# Revit family: VENTS-VS
name_source: partatom
category: Mechanical Equipment
units: mm (PartAtom-declared; Revit-internal decimal feet)

## family parameters
Always vertical = Yes
Classification = None
Cut with Voids When Loaded = No
OmniClass Number = 23.75.35.17.11
OmniClass Title = Fans for Air Ductwork
Part Type = Breaks Into
Room Calculation Point = No
Round Connector Dimension = Use Diameter
Shared = No
Work Plane-Based = No

## types (19) — shared parameters
Casing Material = Fan Zinc
Description = Inline centrifugal fan in sound insulated casing
Family Version = 1.0
Load Classification = HVAC
Maintenance Zone Material = Maintenance Zone
Manufacturer = Vents
Plastic Material = Polypropylene Black
Power Factor = 1
Protection rating = IPX4
URL = https://ventilation-system.com
eH = 75 mm
eL = 75 mm

## per-type parameters (varying)
| type | A | Apparent Power | Connection H | Connection W | Current | Din | Maintenance Zone Depth | Maximum Air Flow Directly | Maximum Air Flow Perpendicularly | Model | Noise Level at 3 m (dBa) | Number of Poles | Power | RPM (min-1) | Transported Air Temperature (°C) | Type Comments | Voltage | Weight | conA | gsD |
| VS 355 4E (50Hz) | 520 mm  [stored 1.70604 ft] | 245 VA | 445 mm  [stored 1.45997 ft] | 445 mm  [stored 1.45997 ft] | 1 A | 260 mm  [stored 0.853018 ft] | 520 mm  [stored 1.70604 ft] | 2650 m³/h | 2890 m³/h | VS 355 4E | 54 | 1 | 245 W | 1420 | -25...+50 | Inline centrifugal fan VS 355 4E | 230 V | 25.00 kg | 260 mm  [stored 0.853018 ft] | 260 mm  [stored 0.853018 ft] |
| VS 355 4D (Star 50Hz) | 520 mm  [stored 1.70604 ft] | 230 VA | 445 mm  [stored 1.45997 ft] | 445 mm  [stored 1.45997 ft] | 1 A | 260 mm  [stored 0.853018 ft] | 520 mm  [stored 1.70604 ft] | 2380 m³/h | 2660 m³/h | VS 355 4D | 53 | 3 | 230 W | 1400 | -25...+70 | Inline centrifugal fan VS 355 4D | 400 V | 25.00 kg | 260 mm  [stored 0.853018 ft] | 260 mm  [stored 0.853018 ft] |
| VS 355 4D (Star 60Hz) | 520 mm  [stored 1.70604 ft] | 235 VA | 445 mm  [stored 1.45997 ft] | 445 mm  [stored 1.45997 ft] | 1 A | 260 mm  [stored 0.853018 ft] | 520 mm  [stored 1.70604 ft] | 2580 m³/h | 2815 m³/h | VS 355 4D | 55 | 3 | 235 W | 1600 | -25...+65 | Inline centrifugal fan VS 355 4D | 400 V | 25.00 kg | 260 mm  [stored 0.853018 ft] | 260 mm  [stored 0.853018 ft] |
| VS 400 4E (50Hz) | 690 mm  [stored 2.26378 ft] | 480 VA | 615 mm  [stored 2.01772 ft] | 615 mm  [stored 2.01772 ft] | 2 A | 345 mm  [stored 1.13189 ft] | 690 mm  [stored 2.26378 ft] | 3535 m³/h | 3750 m³/h | VS 400 4E | 51 | 1 | 480 W | 1370 | -40...+80 | Inline centrifugal fan VS 400 4E | 230 V | 39.00 kg | 345 mm  [stored 1.13189 ft] | 345 mm  [stored 1.13189 ft] |
| VS 400 4E (60Hz) | 690 mm  [stored 2.26378 ft] | 700 VA | 615 mm  [stored 2.01772 ft] | 615 mm  [stored 2.01772 ft] | 3 A | 345 mm  [stored 1.13189 ft] | 690 mm  [stored 2.26378 ft] | 4015 m³/h | 4310 m³/h | VS 400 4E | 52 | 1 | 700 W | 1460 | -40...+55 | Inline centrifugal fan VS 400 4E | 230 V | 39.00 kg | 345 mm  [stored 1.13189 ft] | 345 mm  [stored 1.13189 ft] |
| VS 400 4D (Delta 50Hz) | 690 mm  [stored 2.26378 ft] | 515 VA | 615 mm  [stored 2.01772 ft] | 615 mm  [stored 2.01772 ft] | 1 A | 345 mm  [stored 1.13189 ft] | 690 mm  [stored 2.26378 ft] | 3740 m³/h | 3950 m³/h | VS 400 4D (Delta) | 51 | 3 | 515 W | 1415 | -40...+60 | Inline centrifugal fan VS 400 4D (Delta) | 400 V | 39.00 kg | 345 mm  [stored 1.13189 ft] | 345 mm  [stored 1.13189 ft] |
| VS 400 4D (Delta 60Hz) | 690 mm  [stored 2.26378 ft] | 750 VA | 615 mm  [stored 2.01772 ft] | 615 mm  [stored 2.01772 ft] | 1 A | 345 mm  [stored 1.13189 ft] | 690 mm  [stored 2.26378 ft] | 4055 m³/h | 4310 m³/h | VS 400 4D (Delta) | 53 | 3 | 750 W | 1610 | -40...+60 | Inline centrifugal fan VS 400 4D (Delta) | 400 V | 39.00 kg | 345 mm  [stored 1.13189 ft] | 345 mm  [stored 1.13189 ft] |
| VS 400 4D (Star 50Hz) | 690 mm  [stored 2.26378 ft] | 385 VA | 615 mm  [stored 2.01772 ft] | 615 mm  [stored 2.01772 ft] | 1 A | 345 mm  [stored 1.13189 ft] | 690 mm  [stored 2.26378 ft] | 3110 m³/h | 3340 m³/h | VS 400 4D (Star) | 47 | 3 | 385 W | 1235 | -40...+80 | Inline centrifugal fan VS 400 4D (Star) | 400 V | 39.00 kg | 345 mm  [stored 1.13189 ft] | 345 mm  [stored 1.13189 ft] |
| VS 400 4D (Star 60Hz) | 690 mm  [stored 2.26378 ft] | 515 VA | 615 mm  [stored 2.01772 ft] | 615 mm  [stored 2.01772 ft] | 1 A | 345 mm  [stored 1.13189 ft] | 690 mm  [stored 2.26378 ft] | 3290 m³/h | 3525 m³/h | VS 400 4D (Star) | 49 | 3 | 515 W | 1220 | -40...+40 | Inline centrifugal fan VS 400 4D (Star) | 400 V | 39.00 kg | 345 mm  [stored 1.13189 ft] | 345 mm  [stored 1.13189 ft] |
| VS 450 4E (50Hz) | 690 mm  [stored 2.26378 ft] | 680 VA | 615 mm  [stored 2.01772 ft] | 615 mm  [stored 2.01772 ft] | 3 A | 345 mm  [stored 1.13189 ft] | 690 mm  [stored 2.26378 ft] | 4930 m³/h | 5630 m³/h | VS 450 4E | 53 | 1 | 680 W | 1250 | -40...+70 | Inline centrifugal fan VS 450 4E | 230 V | 43.00 kg | 345 mm  [stored 1.13189 ft] | 345 mm  [stored 1.13189 ft] |
| VS 450 4D (50Hz) | 690 mm  [stored 2.26378 ft] | 740 VA | 615 mm  [stored 2.01772 ft] | 615 mm  [stored 2.01772 ft] | 2 A | 345 mm  [stored 1.13189 ft] | 690 mm  [stored 2.26378 ft] | 5080 m³/h | 5700 m³/h | VS 450 4D | 54 | 3 | 740 W | 1350 | -40...+80 | Inline centrifugal fan VS 450 4D | 400 V | 43.00 kg | 345 mm  [stored 1.13189 ft] | 345 mm  [stored 1.13189 ft] |
| VS 500 4E (50Hz) | 690 mm  [stored 2.26378 ft] | 1300 VA | 615 mm  [stored 2.01772 ft] | 615 mm  [stored 2.01772 ft] | 6 A | 345 mm  [stored 1.13189 ft] | 690 mm  [stored 2.26378 ft] | 6680 m³/h | 7330 m³/h | VS 500 4E | 55 | 1 | 1300 W | 1320 | -20...+50 | Inline centrifugal fan VS 500 4E | 230 V | 52.00 kg | 345 mm  [stored 1.13189 ft] | 345 mm  [stored 1.13189 ft] |
| VS 500 4D (50Hz) | 690 mm  [stored 2.26378 ft] | 1430 VA | 615 mm  [stored 2.01772 ft] | 615 mm  [stored 2.01772 ft] | 3 A | 345 mm  [stored 1.13189 ft] | 690 mm  [stored 2.26378 ft] | 7200 m³/h | 7940 m³/h | VS 500 4D | 58 | 3 | 1430 W | 1375 | -40...+80 | Inline centrifugal fan VS 500 4D | 400 V | 56.00 kg | 345 mm  [stored 1.13189 ft] | 345 mm  [stored 1.13189 ft] |
| VS 560 4D (50Hz) | 820 mm  [stored 2.69029 ft] | 2380 VA | 745 mm  [stored 2.44423 ft] | 745 mm  [stored 2.44423 ft] | 5 A | 410 mm  [stored 1.34514 ft] | 820 mm  [stored 2.69029 ft] | 10490 m³/h | 11340 m³/h | VS 560 4D | 56 | 3 | 2380 W | 1365 | -40...+60 | Inline centrifugal fan VS 560 4D | 400 V | 99.00 kg | 410 mm  [stored 1.34514 ft] | 410 mm  [stored 1.34514 ft] |
| VS 560 6D (50Hz) | 820 mm  [stored 2.69029 ft] | 780 VA | 745 mm  [stored 2.44423 ft] | 745 mm  [stored 2.44423 ft] | 2 A | 410 mm  [stored 1.34514 ft] | 820 mm  [stored 2.69029 ft] | 7330 m³/h | 7970 m³/h | VS 560 6D | 49 | 3 | 780 W | 885 | -40...+55 | Inline centrifugal fan VS 560 6D | 400 V | 86.00 kg | 410 mm  [stored 1.34514 ft] | 410 mm  [stored 1.34514 ft] |
| VS 630 4D (50Hz) | 820 mm  [stored 2.69029 ft] | 3310 VA | 745 mm  [stored 2.44423 ft] | 745 mm  [stored 2.44423 ft] | 6 A | 410 mm  [stored 1.34514 ft] | 820 mm  [stored 2.69029 ft] | 13740 m³/h | 15170 m³/h | VS 630 4D | 67 | 3 | 3310 W | 1170 | -40...+35 | Inline centrifugal fan VS 630 4D | 400 V | 102.00 kg | 410 mm  [stored 1.34514 ft] | 410 mm  [stored 1.34514 ft] |
| VS 630 S 4D (50Hz) | 820 mm  [stored 2.69029 ft] | 4250 VA | 745 mm  [stored 2.44423 ft] | 745 mm  [stored 2.44423 ft] | 8 A | 410 mm  [stored 1.34514 ft] | 820 mm  [stored 2.69029 ft] | 14930 m³/h | 16870 m³/h | VS 630 S 4D | 69 | 3 | 4250 W | 1300 | -40...+60 | Inline centrifugal fan VS 630 S 4D | 400 V | 100.00 kg | 410 mm  [stored 1.34514 ft] | 410 mm  [stored 1.34514 ft] |
| VS 630 6D (50Hz) | 820 mm  [stored 2.69029 ft] | 1310 VA | 745 mm  [stored 2.44423 ft] | 745 mm  [stored 2.44423 ft] | 3 A | 410 mm  [stored 1.34514 ft] | 820 mm  [stored 2.69029 ft] | 10440 m³/h | 12030 m³/h | VS 630 6D | 55 | 3 | 1310 W | 880 | -40...+60 | Inline centrifugal fan VS 630 6D | 400 V | 98.00 kg | 410 mm  [stored 1.34514 ft] | 410 mm  [stored 1.34514 ft] |
| VS 710 6D (50Hz) | 1020 mm  [stored 3.34646 ft] | 2000 VA | 945 mm  [stored 3.10039 ft] | 945 mm  [stored 3.10039 ft] | 4 A | 510 mm  [stored 1.67323 ft] | 1020 mm  [stored 3.34646 ft] | 14880 m³/h | 15830 m³/h | VS 710 6D | 59 | 3 | 2000 W | 890 | -20...+40 | Inline centrifugal fan VS 710 6D | 400 V | 136.00 kg | 510 mm  [stored 1.67323 ft] | 510 mm  [stored 1.67323 ft] |

note: [stored X ft] marks values corroborated as IEEE doubles in the binary element streams (Revit-internal decimal feet)

## geometry (parser evidence)
native form markers: Sweep x11
no freeform markers — native parametric forms only
